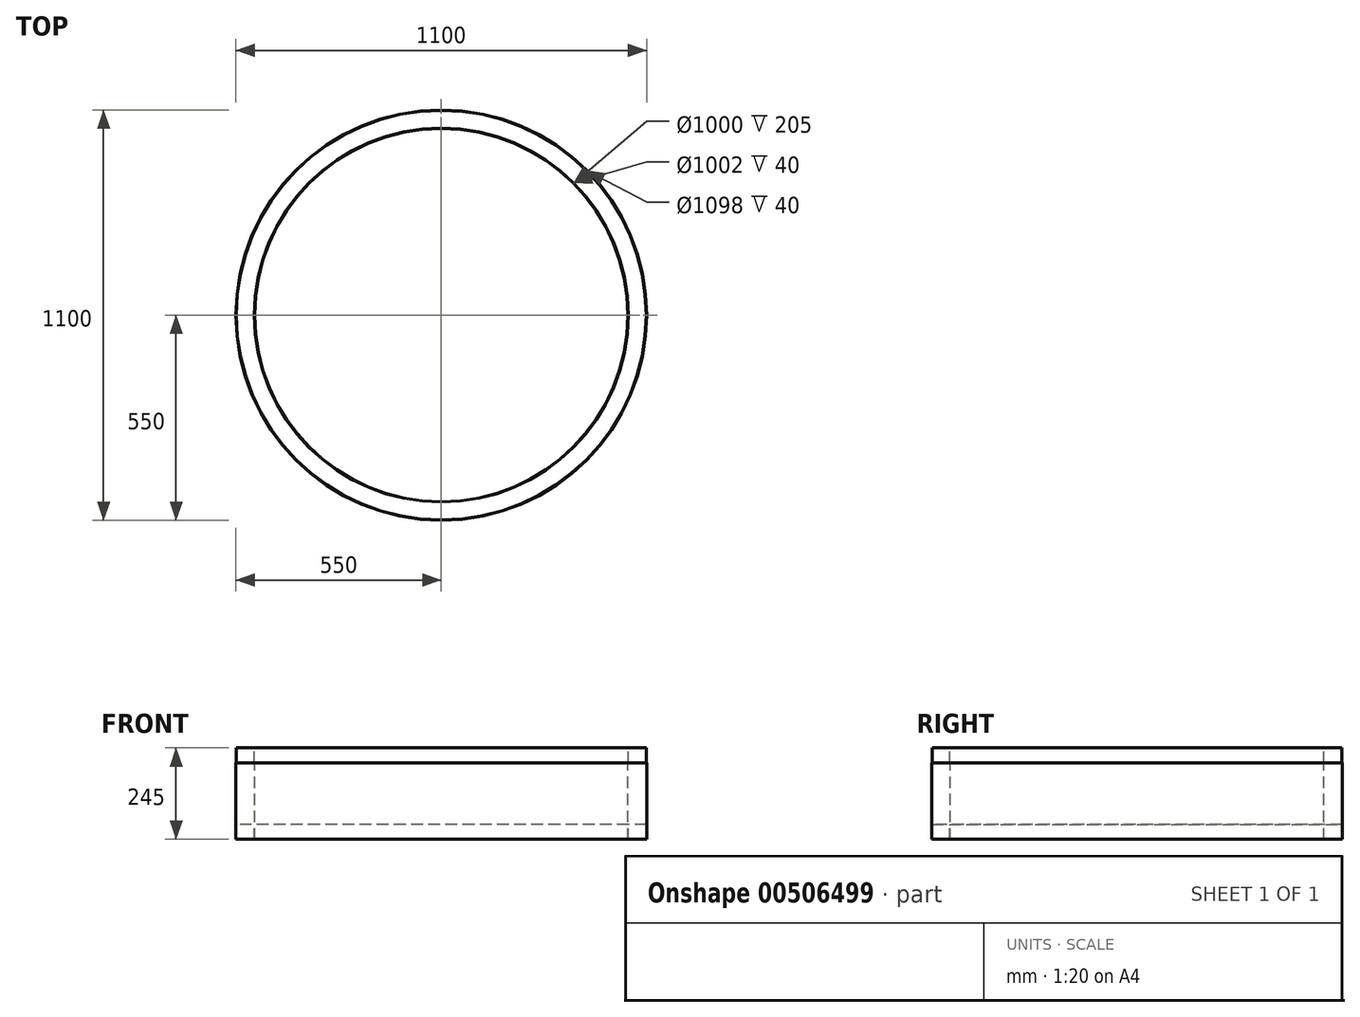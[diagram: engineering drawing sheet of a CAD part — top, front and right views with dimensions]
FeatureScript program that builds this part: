
annotation { "Feature Type Name" : "Feature", "Feature Type Description" : "" }
export const myFeature = defineFeature(function(context is Context, id is Id, definition is map)
    precondition{}
    {
        {
            var Q0;
            Q0=qCreatedBy(makeId("Front.planeOp"),FACE);
            var sketch = newSketch(context, id + "F0", { "sketchPlane" : qUnion([Q0])});
            skLineSegment(sketch, "E0", {"start": v(0, 74.87) * mm, "end": v(0, -73.71) * mm, "construction": true});
            skLineSegment(sketch, "E1", {"start": v(0, 374.84) * mm, "end": v(0, -528.94) * mm, "construction": true});
            skLineSegment(sketch, "E2", {"start": v(-500, -489.75) * mm, "end": v(-500, -284.75) * mm});
            skLineSegment(sketch, "E3", {"start": v(-500, -284.75) * mm, "end": v(-501, -284.75) * mm});
            skLineSegment(sketch, "E4", {"start": v(-501, -284.75) * mm, "end": v(-501, -244.75) * mm});
            skLineSegment(sketch, "E5", {"start": v(-501, -244.75) * mm, "end": v(-549, -244.75) * mm});
            skLineSegment(sketch, "E6", {"start": v(-549, -244.75) * mm, "end": v(-549, -284.75) * mm});
            skLineSegment(sketch, "E7", {"start": v(-549, -284.75) * mm, "end": v(-550, -284.75) * mm});
            skLineSegment(sketch, "E8", {"start": v(-550, -284.75) * mm, "end": v(-550, -489.75) * mm});
            skLineSegment(sketch, "E9", {"start": v(-550, -489.75) * mm, "end": v(-549, -489.75) * mm});
            skLineSegment(sketch, "E10", {"start": v(-549, -489.75) * mm, "end": v(-549, -449.75) * mm});
            skLineSegment(sketch, "E11", {"start": v(-549, -449.75) * mm, "end": v(-501, -449.75) * mm});
            skLineSegment(sketch, "E12", {"start": v(-501, -449.75) * mm, "end": v(-501, -489.75) * mm});
            skLineSegment(sketch, "E13", {"start": v(-501, -489.75) * mm, "end": v(-500, -489.75) * mm});
            skSolve(sketch);
        }
        {
            var Q0;
            Q0=qSketchRegion(id+"F0",true);
            var Q1;
            Q1=sQuery(id+"F0.wireOp",EDGE,"E1");
            revolve(context, id + "F1", {"entities" : qUnion([Q0]), "axis" : qUnion([Q1]), "revolveType" : RevolveType.FULL});
        }
    });
